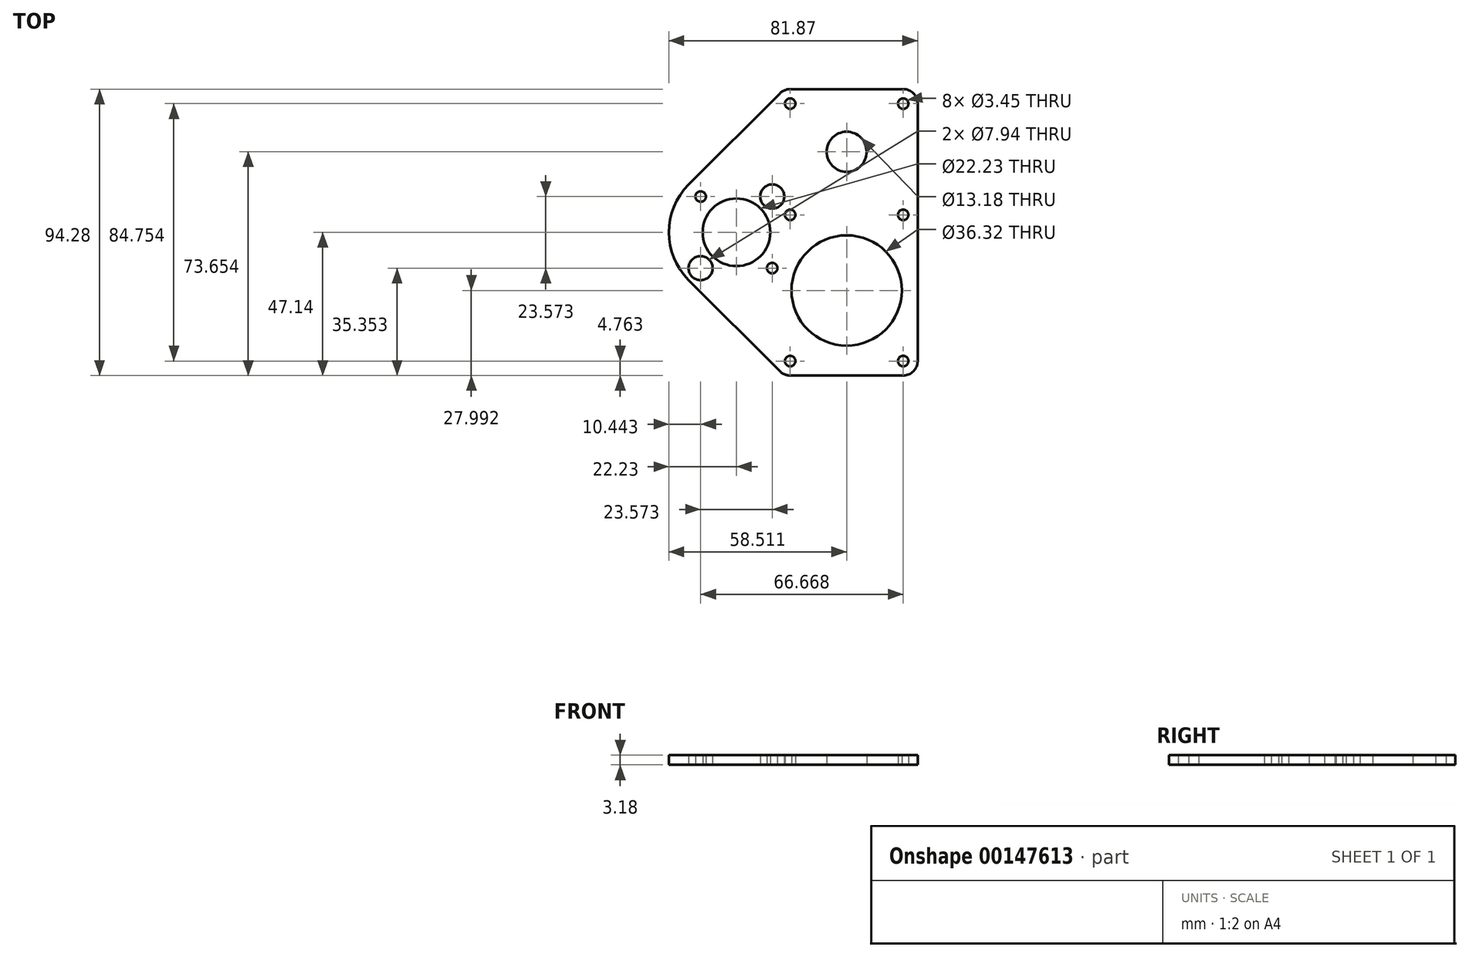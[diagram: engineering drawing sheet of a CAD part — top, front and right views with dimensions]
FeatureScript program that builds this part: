
annotation { "Feature Type Name" : "Feature", "Feature Type Description" : "" }
export const myFeature = defineFeature(function(context is Context, id is Id, definition is map)
    precondition{}
    {
        {
            var Q0;
            Q0=qCreatedBy(makeId("Top.planeOp"),FACE);
            var sketch = newSketch(context, id + "F0", { "sketchPlane" : qUnion([Q0])});
            skPoint(sketch, "E0.rect.middle", {"position": v(0, 0) * mm});
            skCircle(sketch, "E1", {"center": v(0, 0) * mm, "radius": 11.11 * mm});
            skLineSegment(sketch, "E2.bottom", {"start": v(11.79, 11.79) * mm, "end": v(-11.79, 11.79) * mm, "construction": true});
            skLineSegment(sketch, "E2.left", {"start": v(11.79, 11.79) * mm, "end": v(11.79, -11.79) * mm, "construction": true});
            skLineSegment(sketch, "E2.right", {"start": v(-11.79, 11.79) * mm, "end": v(-11.79, -11.79) * mm, "construction": true});
            skCircle(sketch, "E3", {"center": v(-11.79, 11.79) * mm, "radius": 1.73 * mm});
            skCircle(sketch, "E4", {"center": v(11.79, 11.79) * mm, "radius": 3.97 * mm});
            skCircle(sketch, "E5", {"center": v(11.79, -11.79) * mm, "radius": 1.73 * mm});
            skCircle(sketch, "E6", {"center": v(-11.79, -11.79) * mm, "radius": 3.97 * mm});
            skLineSegment(sketch, "E7", {"start": v(-11.79, -11.79) * mm, "end": v(11.79, -11.79) * mm, "construction": true});
            skLineSegment(sketch, "E8", {"start": v(0, 0) * mm, "end": v(36.28, 0) * mm, "construction": true});
            skLineSegment(sketch, "E9", {"start": v(36.28, 11.78) * mm, "end": v(36.28, -11.78) * mm, "construction": true});
            skLineSegment(sketch, "E10", {"start": v(36.28, 0) * mm, "end": v(59.64, 0) * mm, "construction": true});
            skLineSegment(sketch, "E11", {"start": v(-15.72, 15.72) * mm, "end": v(14.31, 45.74) * mm});
            skLineSegment(sketch, "E12", {"start": v(-15.72, -15.72) * mm, "end": v(14.31, -45.74) * mm});
            skLineSegment(sketch, "E13", {"start": v(36.28, 11.78) * mm, "end": v(36.28, 26.51) * mm, "construction": true});
            skLineSegment(sketch, "E14", {"start": v(36.28, -11.78) * mm, "end": v(36.28, -26.51) * mm, "construction": true});
            skCircle(sketch, "E15.cCircle", {"center": v(36.28, 19.15) * mm, "radius": 13.2 * mm, "construction": true});
            skLineSegment(sketch, "E15.0", {"start": v(43.9, 32.35) * mm, "end": v(51.52, 19.15) * mm, "construction": true});
            skLineSegment(sketch, "E15.1", {"start": v(51.52, 19.15) * mm, "end": v(43.9, 5.95) * mm, "construction": true});
            skLineSegment(sketch, "E15.2", {"start": v(43.9, 5.95) * mm, "end": v(28.66, 5.95) * mm, "construction": true});
            skLineSegment(sketch, "E15.3", {"start": v(28.66, 5.95) * mm, "end": v(21.04, 19.15) * mm, "construction": true});
            skLineSegment(sketch, "E15.4", {"start": v(21.04, 19.15) * mm, "end": v(28.66, 32.35) * mm, "construction": true});
            skLineSegment(sketch, "E15.5", {"start": v(28.66, 32.35) * mm, "end": v(43.9, 32.35) * mm, "construction": true});
            skPoint(sketch, "E15.0.midPoint", {"position": v(47.71, 25.75) * mm});
            skCircle(sketch, "E16", {"center": v(36.28, 19.15) * mm, "radius": 18.16 * mm, "construction": true});
            skCircle(sketch, "E17", {"center": v(43.9, 32.35) * mm, "radius": 2.92 * mm, "construction": true});
            skCircle(sketch, "E18", {"center": v(17.68, 42.38) * mm, "radius": 1.73 * mm});
            skCircle(sketch, "E19", {"center": v(54.88, 5.75) * mm, "radius": 1.73 * mm});
            skCircle(sketch, "E20", {"center": v(17.68, 5.75) * mm, "radius": 1.73 * mm});
            skArc(sketch, "E21", {"start": v(17.68, 47.14) * mm, "mid": v(15.86, 46.78) * mm, "end": v(14.31, 45.74) * mm});
            skLineSegment(sketch, "E22", {"start": v(17.68, 47.14) * mm, "end": v(59.64, 47.14) * mm});
            skLineSegment(sketch, "E23", {"start": v(59.64, 47.14) * mm, "end": v(59.64, -47.14) * mm});
            skLineSegment(sketch, "E24", {"start": v(59.64, -47.14) * mm, "end": v(17.68, -47.14) * mm});
            skArc(sketch, "E25", {"start": v(14.31, -45.74) * mm, "mid": v(15.86, -46.78) * mm, "end": v(17.68, -47.14) * mm});
            skLineSegment(sketch, "E26", {"start": v(36.28, 26.51) * mm, "end": v(36.28, 47.14) * mm, "construction": true});
            skLineSegment(sketch, "E27.bottom", {"start": v(17.68, 42.38) * mm, "end": v(54.88, 42.38) * mm, "construction": true});
            skLineSegment(sketch, "E27.top", {"start": v(17.68, 5.75) * mm, "end": v(54.88, 5.75) * mm, "construction": true});
            skLineSegment(sketch, "E27.left", {"start": v(17.68, 42.38) * mm, "end": v(17.68, 5.75) * mm, "construction": true});
            skLineSegment(sketch, "E27.right", {"start": v(54.88, 42.38) * mm, "end": v(54.88, 5.75) * mm, "construction": true});
            skArc(sketch, "E28", {"start": v(54.88, 0.99) * mm, "mid": v(58.25, 2.38) * mm, "end": v(59.64, 5.75) * mm, "construction": true});
            skLineSegment(sketch, "E29", {"start": v(54.88, 0.99) * mm, "end": v(36.28, 0.99) * mm, "construction": true});
            skArc(sketch, "E30", {"start": v(59.64, 5.75) * mm, "mid": v(51.51, 9.12) * mm, "end": v(54.88, 0.99) * mm, "construction": true});
            skPoint(sketch, "E31", {"position": v(36.28, 42.38) * mm});
            skCircle(sketch, "E32", {"center": v(36.28, 26.51) * mm, "radius": 6.59 * mm});
            skCircle(sketch, "E33", {"center": v(54.88, 42.38) * mm, "radius": 1.73 * mm});
            skCircle(sketch, "E34", {"center": v(36.28, -19.15) * mm, "radius": 18.16 * mm});
            skArc(sketch, "E35", {"start": v(-15.72, 15.72) * mm, "mid": v(-22.22, 0) * mm, "end": v(-15.72, -15.72) * mm});
            skCircle(sketch, "E36", {"center": v(-11.79, -11.79) * mm, "radius": 5.56 * mm, "construction": true});
            skCircle(sketch, "E37", {"center": v(17.68, -42.38) * mm, "radius": 1.73 * mm});
            skLineSegment(sketch, "E38", {"start": v(17.68, -42.38) * mm, "end": v(54.88, -42.38) * mm, "construction": true});
            skLineSegment(sketch, "E39", {"start": v(54.88, -42.38) * mm, "end": v(59.64, -42.38) * mm, "construction": true});
            skLineSegment(sketch, "E40", {"start": v(54.88, 42.38) * mm, "end": v(54.88, 47.14) * mm, "construction": true});
            skLineSegment(sketch, "E41", {"start": v(54.88, 42.38) * mm, "end": v(59.64, 42.38) * mm, "construction": true});
            skCircle(sketch, "E42", {"center": v(54.88, -42.38) * mm, "radius": 1.73 * mm});
            skSolve(sketch);
        }
        {
            var Q0;
            Q0=qSketchRegion(id+"F0",true);
            extrude(context, id + "F1", {"entities" : qUnion([Q0]), "depth" : 3.17 * mm});
        }
        {
            var Q0;
            Q0=makeQuery(id+"F1.opExtrude","SWEPT_EDGE",EDGE,{"disambiguationData":[OSD([sQuery(id+"F0.wireOp",EDGE,"E22"),sQuery(id+"F0.wireOp",EDGE,"E23")])]});
            var Q1;
            Q1=makeQuery(id+"F1.opExtrude","SWEPT_EDGE",EDGE,{"disambiguationData":[OSD([sQuery(id+"F0.wireOp",EDGE,"E23"),sQuery(id+"F0.wireOp",EDGE,"E24")])]});
            fillet(context, id + "F2", {"entities" : qUnion([Q0, Q1]), "radius" : 4.76 * mm, "tangentPropagation" : true, "allowEdgeOverflow" : false});
        }
    });
